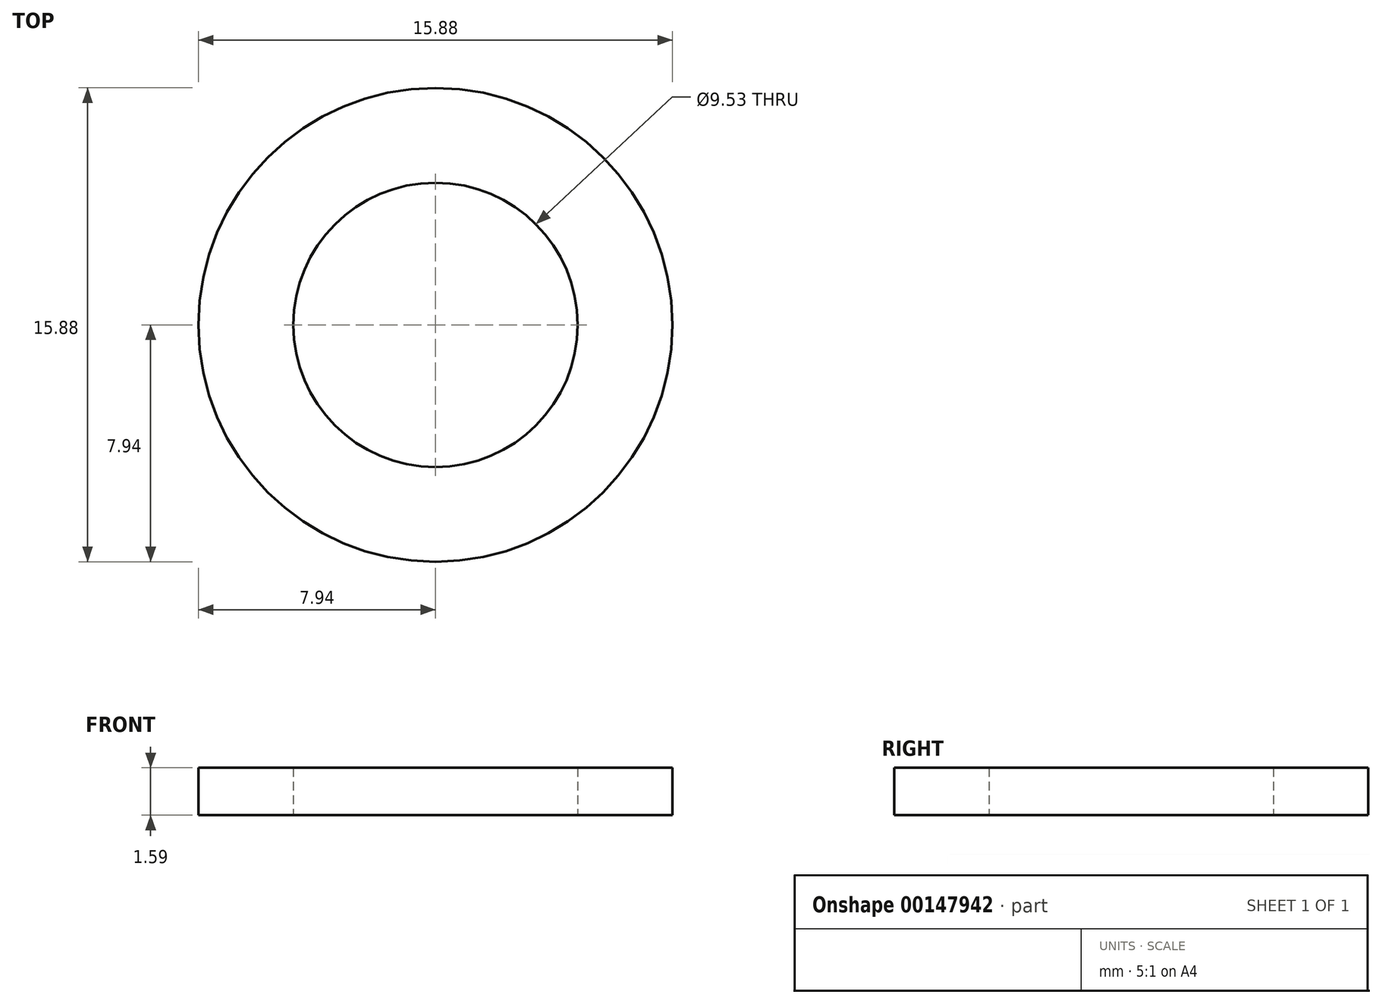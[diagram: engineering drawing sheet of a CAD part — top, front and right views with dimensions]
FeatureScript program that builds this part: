
annotation { "Feature Type Name" : "Feature", "Feature Type Description" : "" }
export const myFeature = defineFeature(function(context is Context, id is Id, definition is map)
    precondition{}
    {
        {
            var Q0;
            Q0=qCreatedBy(makeId("Top.planeOp"),FACE);
            var sketch = newSketch(context, id + "F0", { "sketchPlane" : qUnion([Q0])});
            skCircle(sketch, "E0", {"center": v(0, 0) * mm, "radius": 4.76 * mm});
            skCircle(sketch, "E1", {"center": v(0, 0) * mm, "radius": 7.94 * mm});
            skSolve(sketch);
        }
        {
            var Q0;
            Q0=qSketchRegion(id+"F0",true);
            extrude(context, id + "F1", {"entities" : qUnion([Q0]), "depth" : 1.59 * mm});
        }
    });
